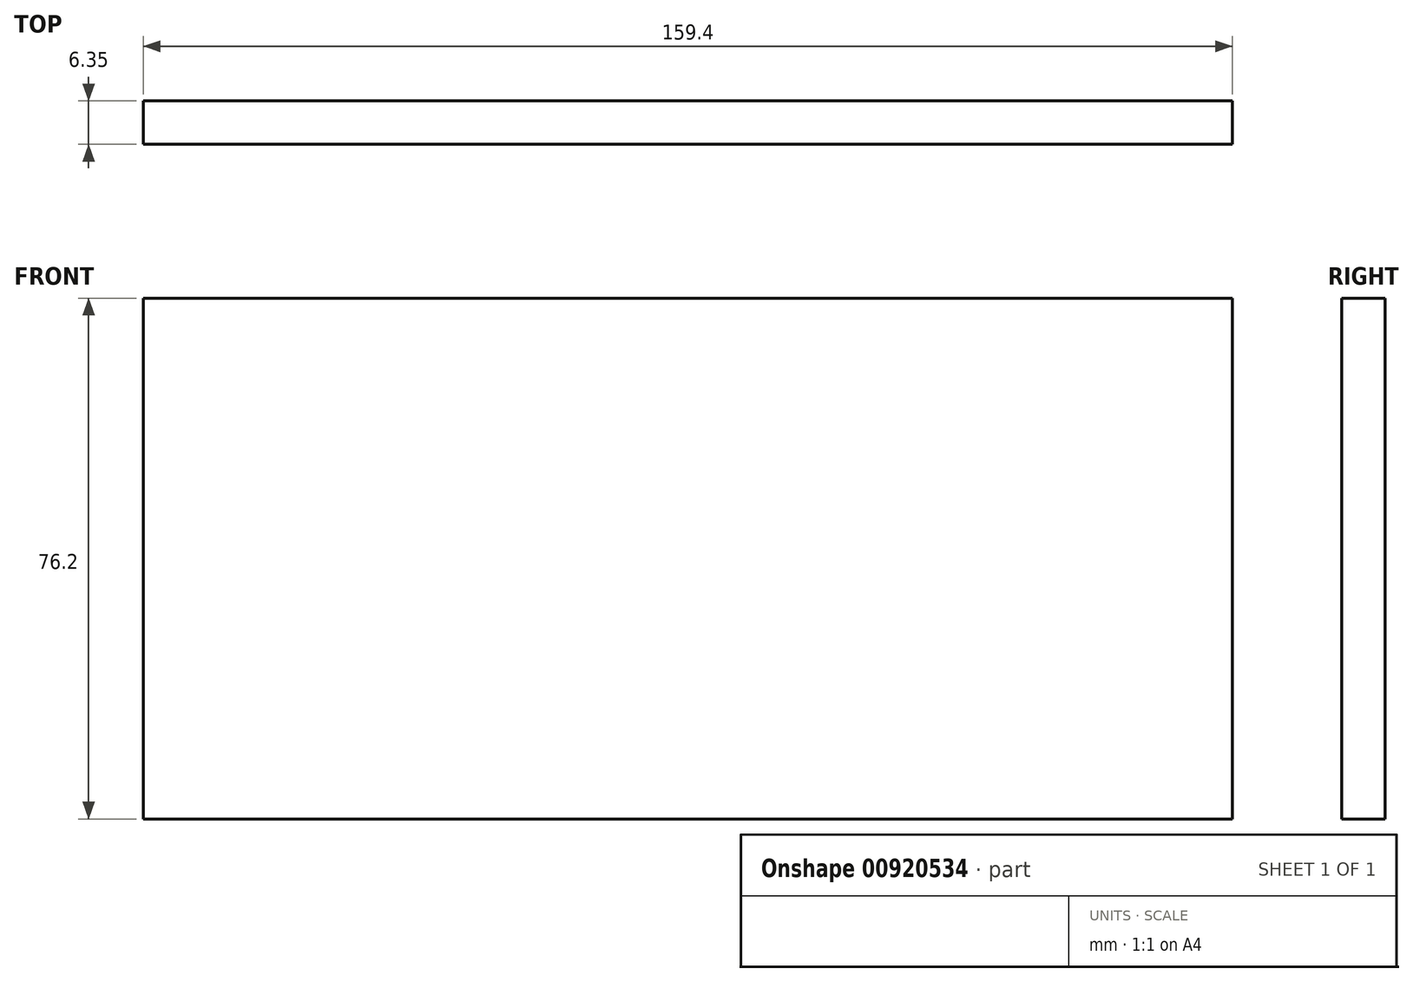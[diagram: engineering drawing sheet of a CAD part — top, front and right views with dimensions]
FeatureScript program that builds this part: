
annotation { "Feature Type Name" : "Feature", "Feature Type Description" : "" }
export const myFeature = defineFeature(function(context is Context, id is Id, definition is map)
    precondition{}
    {
        {
            var Q0;
            Q0=qCreatedBy(makeId("Front.planeOp"),FACE);
            var sketch = newSketch(context, id + "F0", { "sketchPlane" : qUnion([Q0])});
            skLineSegment(sketch, "E0.bottom", {"start": v(0, 38.1) * mm, "end": v(159.4, 38.1) * mm});
            skLineSegment(sketch, "E0.top", {"start": v(0, -38.1) * mm, "end": v(159.4, -38.1) * mm});
            skLineSegment(sketch, "E0.left", {"start": v(0, 38.1) * mm, "end": v(0, -38.1) * mm});
            skLineSegment(sketch, "E0.right", {"start": v(159.4, 38.1) * mm, "end": v(159.4, -38.1) * mm});
            skSolve(sketch);
        }
        {
            var Q0;
            Q0=makeQuery(id+"F0.imprint","IMPRINT",FACE,{"disambiguationData":[TD([[makeQuery(id+"F0.imprint","IMPRINT",EDGE,{"derivedFrom":sQuery(id+"F0.wireOp",EDGE,"E0.bottom")}),-1.0]])]});
            extrude(context, id + "F1", {"entities" : qUnion([Q0]), "oppositeDirection" : true, "depth" : 6.35 * mm, "offsetDistance" : 25.4 * mm});
        }
    });
